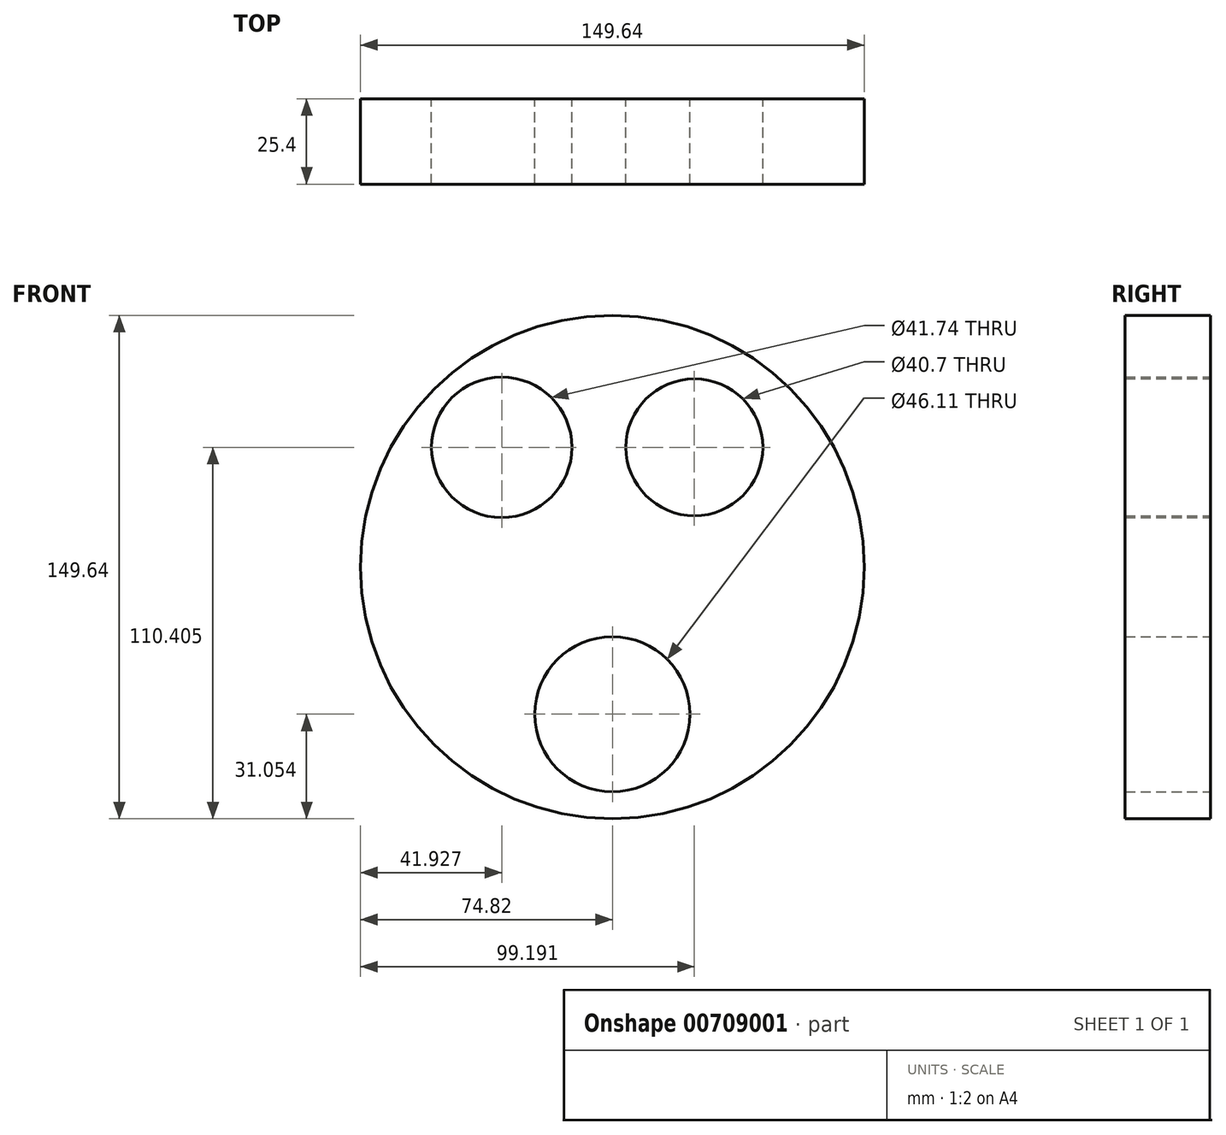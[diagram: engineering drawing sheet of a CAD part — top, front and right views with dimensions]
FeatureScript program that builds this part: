
annotation { "Feature Type Name" : "Feature", "Feature Type Description" : "" }
export const myFeature = defineFeature(function(context is Context, id is Id, definition is map)
    precondition{}
    {
        {
            var Q0;
            Q0=qCreatedBy(makeId("Front.planeOp"),FACE);
            var sketch = newSketch(context, id + "F0", { "sketchPlane" : qUnion([Q0])});
            skCircle(sketch, "E0", {"center": v(0, 0) * mm, "radius": 74.82 * mm});
            skCircle(sketch, "E1", {"center": v(-32.9, 35.59) * mm, "radius": 20.87 * mm});
            skCircle(sketch, "E2", {"center": v(24.37, 35.59) * mm, "radius": 20.35 * mm});
            skCircle(sketch, "E3", {"center": v(0, -43.77) * mm, "radius": 23.05 * mm});
            skSolve(sketch);
        }
        {
            var Q0;
            Q0=makeQuery(id+"F0.imprint","IMPRINT",FACE,{"disambiguationData":[TD([[makeQuery(id+"F0.imprint","IMPRINT",EDGE,{"derivedFrom":sQuery(id+"F0.wireOp",EDGE,"E0")}),1.0]])]});
            extrude(context, id + "F1", {"entities" : qUnion([Q0]), "depth" : 25.4 * mm, "offsetDistance" : 25.4 * mm});
        }
    });
